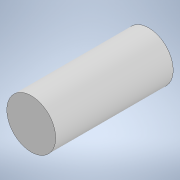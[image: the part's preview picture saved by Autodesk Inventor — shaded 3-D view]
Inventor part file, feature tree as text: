
AUTODESK INVENTOR PART (.ipt)
format: ipt  version: 2022 (Build 260153000, 153)  size: 90,112 bytes
history: native  units: in
note: dims shown in document units (in); Inventor stores cm internally (conversion verified against a paired STEP export)
features: extrude x1, sketch x1
ambient origin geometry x8: Origin, YZ Plane, XZ Plane, XY Plane, X Axis, Y Axis, Z Axis, Center Point
bodies: Solid1 (feature_tree)
feature tree (2):
  extrude  "Extrusion1"  Depth=1.25in TaperAngle=0.0deg
  sketch  "Sketch1"  dims[d0=0.52in d1=1.25in d2=0.0in]
